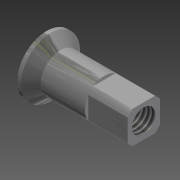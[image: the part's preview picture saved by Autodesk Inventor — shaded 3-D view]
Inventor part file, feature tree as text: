
AUTODESK INVENTOR PART (.ipt)
format: ipt  version: 2015 (Build 190159000, 159)  size: 188,928 bytes
history: native  units: mm
features: sketch x4, extrude x2, chamfer x2, other x1, revolve x1, hole x1, thread x1, projected_geometry x1
ambient origin geometry x8: Origin, YZ Plane, XZ Plane, XY Plane, X Axis, Y Axis, Z Axis, Center Point
bodies: Body1 (feature_tree)
feature tree (13):
  other  "Bryła1"
  revolve  "Obrót1"
  extrude  "Wyciągnięcie proste2"  Depth=11.0mm
  hole  "Otwór1"  [1 undecoded]
  chamfer  "Faza1"  Distance=10.0mm
  chamfer  "Faza2"  Distance=2.5mm
  extrude  "Wyciągnięcie proste3"  TaperAngle=45.0deg  [1 undecoded]
  thread  "Gwint1"
  sketch  "Szkic1"
  sketch  "Szkic2"
  sketch  "Szkic3"
  projected_geometry  "Pętla rzutowana1"
  sketch  "Szkic5"
note: 2 required parameter values undecoded (feature->parameter linkage not recoverable at this tier; creation-order binding heuristic only, values carry confidence <= 0.55)
